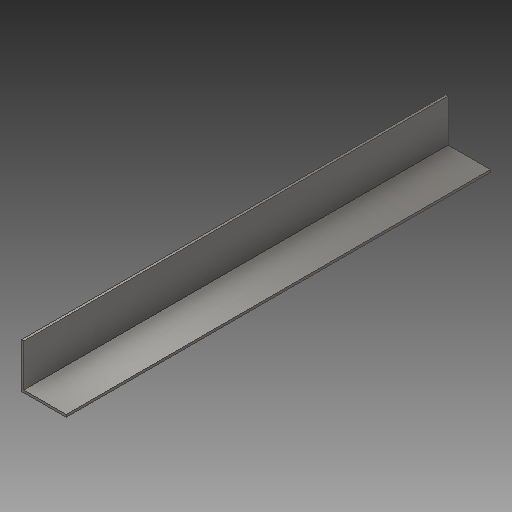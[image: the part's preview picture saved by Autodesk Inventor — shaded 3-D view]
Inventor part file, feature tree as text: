
AUTODESK INVENTOR PART (.ipt)
format: ipt  version: 2017 (Build 210142000, 142)  size: 106,496 bytes
history: native  units: in
note: dims shown in document units (in); Inventor stores cm internally (conversion verified against a paired STEP export)
features: other x3, sketch x2
ambient origin geometry x8: Origin, YZ Plane, XZ Plane, XY Plane, X Axis, Y Axis, Z Axis, Center Point
bodies: Solid1 (feature_tree)
feature tree (5):
  other  "Long Boi.ipt"
  other  "Solid1::Long Boi.ipt"
  other  "TaggingFeature1"
  sketch  "Sketch1"  dims[d0=0.3937in]
  sketch  "Sketch2"
